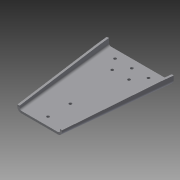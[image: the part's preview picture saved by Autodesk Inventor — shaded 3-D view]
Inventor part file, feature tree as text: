
AUTODESK INVENTOR PART (.ipt)
format: ipt  version: 2013 (Build 170138000, 138)  size: 207,872 bytes
history: native  units: in
note: dims shown in document units (in); Inventor stores cm internally (conversion verified against a paired STEP export)
features: sheet_metal_op x4, sketch x3, other x3, chamfer x1, mirror x1, hole x1
ambient origin geometry x8: Origin, YZ Plane, XZ Plane, XY Plane, X Axis, Y Axis, Z Axis, Center Point
bodies: Solid1 (feature_tree)
feature tree (13):
  sheet_metal_op  "Face1"
  sheet_metal_op  "Flange1"
  chamfer  "Chamfer1"  Distance=0.1875in
  mirror  "Mirror1"
  hole  "Hole1"  [1 undecoded]
  sketch  "Sketch1"  dims[d0=3.0in]
  other  "Plate1"
  sketch  "Sketch2"  dims[d1=9.0in]
  other  "Plate2"
  sheet_metal_op  "Bend1"
  sheet_metal_op  "Corner1"
  sketch  "Sketch3"  dims[d2=1.0in d3=0.1875in d4=0.1875in d5=0.0938in d6=0.375in d7=0.1875in d8=0.75in d9=90.0deg d10=0.1875in d11=0.75in d12=0.1875in d13=0.1875in d14=8.0623in d15=0.25in d16=45.0deg d17=1.5in d19=1.5in d20=0.75in d21=0.75in d24=1.0in d25=0.75in d26=0.25in d27=0.75in d28=0.375in d29=0.25in d30=0.5635in d31=0.1875in d32=0.8108in d33=0.75in d34=2.0in d35=3.0in]
  other  "Definition1"
note: 1 required parameter value undecoded (feature->parameter linkage not recoverable at this tier; creation-order binding heuristic only, values carry confidence <= 0.55)
